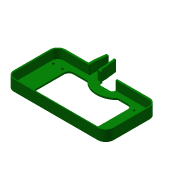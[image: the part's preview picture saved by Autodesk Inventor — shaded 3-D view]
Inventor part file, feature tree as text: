
AUTODESK INVENTOR PART (.ipt)
format: ipt  version: 2015 (Build 190159000, 159)  size: 290,304 bytes
history: native  units: in
note: dims shown in document units (in); Inventor stores cm internally (conversion verified against a paired STEP export)
features: extrude x11, sketch x11, fillet x7
ambient origin geometry x8: Origin, YZ Plane, XZ Plane, XY Plane, X Axis, Y Axis, Z Axis, Center Point
bodies: Solid1 (feature_tree)
feature tree (29):
  extrude  "Extrusion1"  Depth=2.655in
  extrude  "Extrusion2"  Depth=0.5in TaperAngle=0.0deg
  fillet  "Fillet1"  Radius=0.09in
  fillet  "Fillet2"  Radius=0.3in
  extrude  "Extrusion3"  Depth=0.42in
  extrude  "Extrusion4"  Depth=0.29in
  extrude  "Extrusion5"  Depth=0.125in
  fillet  "Fillet3"  Radius=0.125in
  fillet  "Fillet4"  Radius=0.125in
  fillet  "Fillet5"  Radius=0.125in
  extrude  "Extrusion6"  Depth=0.125in TaperAngle=0.0deg
  fillet  "Fillet6"  Radius=0.06in
  extrude  "Extrusion7"  Depth=0.04in
  extrude  "Extrusion8"  Depth=0.25in
  fillet  "Fillet7"  [1 undecoded]
  extrude  "Extrusion10"  Depth=0.16in
  extrude  "Extrusion11"  Depth=4.4in
  extrude  "Extrusion12"  Depth=0.9in
  sketch  "Sketch1"  dims[d0=5.265in d1=2.655in]
  sketch  "Sketch2"  dims[d2=0.08in d3=0.5in d4=0.0in d5=0.09in d6=0.0in d7=0.3in]
  sketch  "Sketch3"  dims[d8=0.425in d9=0.42in]
  sketch  "Sketch4"  dims[d10=0.125in d11=0.0in d14=0.29in]
  sketch  "Sketch5"  dims[d15=0.9in d17=0.125in d18=0.125in d19=0.125in d20=0.125in]
  sketch  "Sketch6"  dims[d21=0.0in d22=0.0in d23=0.125in d24=0.0in d25=0.06in]
  sketch  "Sketch7"  dims[d26=0.06in d27=0.04in]
  sketch  "Sketch8"  dims[d29=0.25in d30=2.75in d31=0.0in d32=0.0in]
  sketch  "Sketch10"  dims[d33=0.16in d34=0.375in]
  sketch  "Sketch11"  dims[d35=0.375in d36=4.4in]
  sketch  "Sketch12"  dims[d37=0.25in d38=0.9in d39=0.9in d40=0.125in d41=0.125in d42=0.0in d43=1.0in d44=0.0in d45=1.1887in d46=1.1887in d47=0.2702in d50=1.932in d53=0.9in d54=0.9in d55=0.3in d56=0.3in d57=0.25in d58=1.0in d59=0.0in d61=0.8in d62=0.48in d63=0.88in d64=0.3in d65=0.0in d66=2.0in d67=0.0in]
note: 1 required parameter value undecoded (feature->parameter linkage not recoverable at this tier; creation-order binding heuristic only, values carry confidence <= 0.55)
